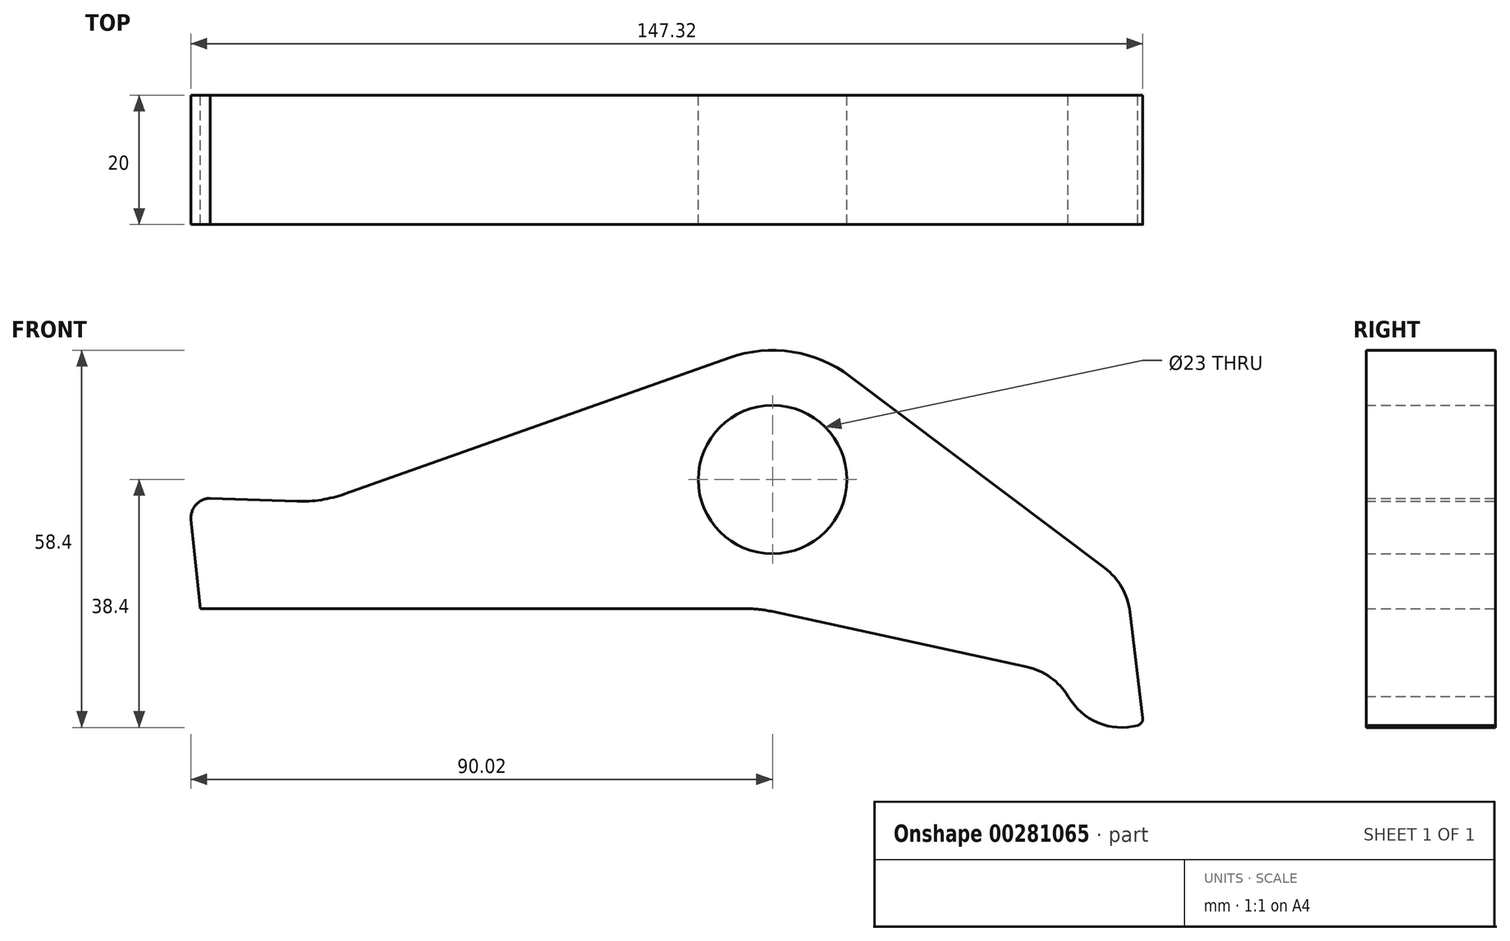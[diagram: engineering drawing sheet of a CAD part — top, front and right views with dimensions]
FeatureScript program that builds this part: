
annotation { "Feature Type Name" : "Feature", "Feature Type Description" : "" }
export const myFeature = defineFeature(function(context is Context, id is Id, definition is map)
    precondition{}
    {
        {
            var Q0;
            Q0=qCreatedBy(makeId("Front.planeOp"),FACE);
            var sketch = newSketch(context, id + "F0", { "sketchPlane" : qUnion([Q0])});
            skCircle(sketch, "E0", {"center": v(0, 0) * mm, "radius": 11.5 * mm});
            skArc(sketch, "E1", {"start": v(-6.68, 18.85) * mm, "mid": v(3.04, 19.77) * mm, "end": v(12.04, 15.97) * mm});
            skLineSegment(sketch, "E2", {"start": v(-6.68, 18.85) * mm, "end": v(-66.22, -2.23) * mm});
            skLineSegment(sketch, "E3", {"start": v(0, 0) * mm, "end": v(-100.7, 0) * mm, "construction": true});
            skLineSegment(sketch, "E4", {"start": v(-90, -6.21) * mm, "end": v(-88.55, -20) * mm});
            skLineSegment(sketch, "E5", {"start": v(-88.55, -20) * mm, "end": v(-4.2, -20) * mm});
            skArc(sketch, "E6.filletArc", {"start": v(-87.02, -2.9) * mm, "mid": v(-89.25, -3.9) * mm, "end": v(-90, -6.21) * mm});
            skLineSegment(sketch, "E7", {"start": v(-87.02, -2.9) * mm, "end": v(-73.6, -3.37) * mm});
            skLineSegment(sketch, "E8", {"start": v(12.04, 15.97) * mm, "end": v(51.42, -13.7) * mm});
            skPoint(sketch, "E9.visualSharp", {"position": v(-69.8, -3.5) * mm});
            skArc(sketch, "E10.filletArc", {"start": v(-73.6, -3.37) * mm, "mid": v(-69.86, -3.15) * mm, "end": v(-66.22, -2.23) * mm});
            skArc(sketch, "E11", {"start": v(56.53, -38.07) * mm, "mid": v(57.12, -37.67) * mm, "end": v(57.3, -36.98) * mm});
            skLineSegment(sketch, "E12", {"start": v(55.33, -20.5) * mm, "end": v(57.3, -36.98) * mm});
            skPoint(sketch, "E13.visualSharp", {"position": v(54.82, -16.27) * mm});
            skArc(sketch, "E13.filletArc", {"start": v(55.33, -20.5) * mm, "mid": v(54.07, -16.7) * mm, "end": v(51.42, -13.7) * mm});
            skArc(sketch, "E14", {"start": v(45.75, -33.57) * mm, "mid": v(43.01, -30.64) * mm, "end": v(39.35, -29.03) * mm});
            skLineSegment(sketch, "E15", {"start": v(0.06, -20.46) * mm, "end": v(39.35, -29.03) * mm});
            skArc(sketch, "E16.trimOffspring", {"start": v(45.75, -33.57) * mm, "mid": v(50.37, -37.66) * mm, "end": v(56.53, -38.07) * mm});
            skPoint(sketch, "E17.visualSharp", {"position": v(-2.04, -20) * mm});
            skArc(sketch, "E17.filletArc", {"start": v(-2.04, -20) * mm, "mid": v(-2.04, -20) * mm, "end": v(-2.05, -20) * mm});
            skArc(sketch, "E18.filletArc", {"start": v(0.06, -20.46) * mm, "mid": v(-2.06, -20.12) * mm, "end": v(-4.2, -20) * mm});
            skLineSegment(sketch, "E19", {"start": v(-90, -6.21) * mm, "end": v(-90, -20) * mm, "construction": true});
            skSolve(sketch);
        }
        {
            var Q0;
            Q0 = qSketchRegion(id + "F0", true);
            extrude(context, id + "F1", {"entities" : qUnion([Q0]), "depth" : 20 * mm});
        }
    });
